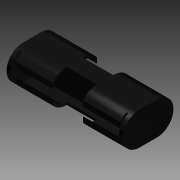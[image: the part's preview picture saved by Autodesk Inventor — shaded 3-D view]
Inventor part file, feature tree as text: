
AUTODESK INVENTOR PART (.ipt)
format: ipt  version: 2014 (Build 180170000, 170)  size: 199,168 bytes
history: native  units: in
note: dims shown in document units (in); Inventor stores cm internally (conversion verified against a paired STEP export)
features: extrude x3, projected_geometry x3, plane x2, sketch x2, fillet x1
ambient origin geometry x8: Origin, YZ Plane, XZ Plane, XY Plane, X Axis, Y Axis, Z Axis, Center Point
bodies: Solid1 (feature_tree)
feature tree (11):
  extrude  "Extrusion1"  Depth=2.3in
  fillet  "Fillet1"  Radius=1.0in
  plane  "Work Plane1"
  sketch  "Sketch2"  dims[d4=0.325in d5=-0.08in d6=0.05in d7=0.05in d8=-0.08in d9=0.04in d10=1.0in d11=0.0in d12=0.32in d17=0.875in d18=0.115in d19=0.115in d20=0.275in d21=0.875in d23=0.6in d24=0.735in d25=0.6in d26=0.735in d27=0.875in d47=1.0in d48=0.0in d49=0.08in d50=0.08in d51=0.015in d52=0.2775in d53=0.2775in d54=0.2775in d55=0.2775in d56=0.035in d57=0.035in d58=0.035in d59=0.035in d60=0.625in d61=0.625in d62=0.735in d63=0.735in d64=0.735in d65=0.735in d66=0.125in d67=0.125in d68=0.125in d69=0.125in d70=0.0625in d71=0.0625in]
  plane  "Work Plane2"
  extrude  "Extrusion2"  [1 undecoded]
  extrude  "Extrusion3"  Depth=0.05in
  sketch  "Sketch1"  dims[d0=0.65in d1=2.3in d2=1.0in d3=0.0in]
  projected_geometry  "Projected Loop1"
  projected_geometry  "Projected Loop2"
  projected_geometry  "Projected Loop3"
note: 1 required parameter value undecoded (feature->parameter linkage not recoverable at this tier; creation-order binding heuristic only, values carry confidence <= 0.55)
